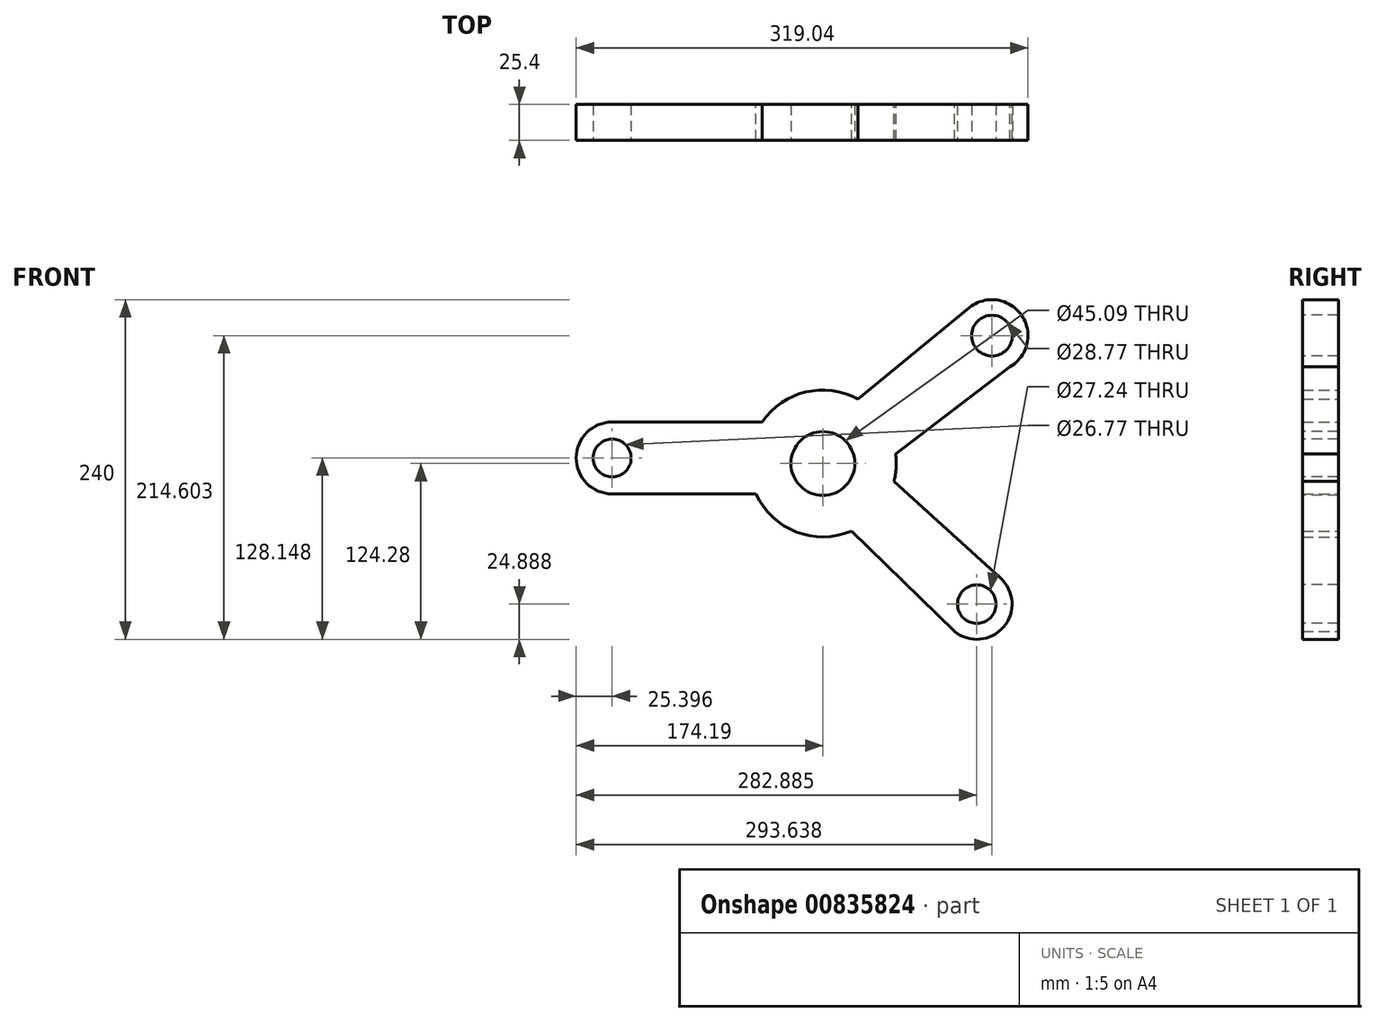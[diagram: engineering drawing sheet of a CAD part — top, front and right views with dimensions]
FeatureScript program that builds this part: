
annotation { "Feature Type Name" : "Feature", "Feature Type Description" : "" }
export const myFeature = defineFeature(function(context is Context, id is Id, definition is map)
    precondition{}
    {
        {
            var Q0;
            Q0=qCreatedBy(makeId("Front.planeOp"),FACE);
            var sketch = newSketch(context, id + "F0", { "sketchPlane" : qUnion([Q0])});
            skCircle(sketch, "E0", {"center": v(0, 0) * mm, "radius": 51.87 * mm});
            skLineSegment(sketch, "E1", {"start": v(24.76, 45.58) * mm, "end": v(103.35, 109.97) * mm});
            skArc(sketch, "E2", {"start": v(132.22, 68.37) * mm, "mid": v(140.32, 104.8) * mm, "end": v(103.35, 109.97) * mm});
            skLineSegment(sketch, "E3", {"start": v(132.22, 68.37) * mm, "end": v(51.43, 6.76) * mm});
            skLineSegment(sketch, "E4", {"start": v(50.32, -12.59) * mm, "end": v(125.45, -80.99) * mm});
            skArc(sketch, "E5", {"start": v(93, -118.71) * mm, "mid": v(127.57, -115.62) * mm, "end": v(125.45, -80.99) * mm});
            skLineSegment(sketch, "E6", {"start": v(93, -118.71) * mm, "end": v(20.3, -47.73) * mm});
            skLineSegment(sketch, "E7", {"start": v(-47.2, -21.53) * mm, "end": v(-148.8, -21.53) * mm});
            skArc(sketch, "E8", {"start": v(-148.8, 29.27) * mm, "mid": v(-174.2, 3.87) * mm, "end": v(-148.8, -21.53) * mm});
            skLineSegment(sketch, "E9", {"start": v(-148.8, 29.27) * mm, "end": v(-42.83, 29.27) * mm});
            skSolve(sketch);
        }
        {
            var Q0;
            Q0 = qSketchRegion(id + "F0", true);
            extrude(context, id + "F1", {"entities" : qUnion([Q0]), "depth" : 25.4 * mm, "offsetDistance" : 25.4 * mm});
        }
        {
            var Q0;
            Q0=makeQuery(id+"F1.opExtrude","CAP_FACE",FACE,{"disambiguationData":[OSD([sQuery(id+"F0.wireOp",EDGE,"E0"),sQuery(id+"F0.wireOp",EDGE,"E1"),sQuery(id+"F0.wireOp",EDGE,"E2"),sQuery(id+"F0.wireOp",EDGE,"E3"),sQuery(id+"F0.wireOp",EDGE,"E4"),sQuery(id+"F0.wireOp",EDGE,"E5"),sQuery(id+"F0.wireOp",EDGE,"E6"),sQuery(id+"F0.wireOp",EDGE,"E7"),sQuery(id+"F0.wireOp",EDGE,"E8"),sQuery(id+"F0.wireOp",EDGE,"E9")])],"isStart":false});
            var sketch = newSketch(context, id + "F2", { "sketchPlane" : qUnion([Q0])});
            skCircle(sketch, "E10", {"center": v(0, 0) * mm, "radius": 22.55 * mm});
            skSolve(sketch);
        }
        {
            var Q0;
            Q0 = qSketchRegion(id + "F2", true);
            extrude(context, id + "F3", {"entities" : qUnion([Q0]), "operationType" : NewBodyOperationType.REMOVE, "endBound" : BoundingType.THROUGH_ALL, "oppositeDirection" : true, "depth" : 25.4 * mm, "offsetDistance" : 25.4 * mm});
        }
        {
            var Q0;
            Q0=makeQuery(id+"F1.opExtrude","CAP_FACE",FACE,{"disambiguationData":[OSD([sQuery(id+"F0.wireOp",EDGE,"E0"),sQuery(id+"F0.wireOp",EDGE,"E1"),sQuery(id+"F0.wireOp",EDGE,"E2"),sQuery(id+"F0.wireOp",EDGE,"E3"),sQuery(id+"F0.wireOp",EDGE,"E4"),sQuery(id+"F0.wireOp",EDGE,"E5"),sQuery(id+"F0.wireOp",EDGE,"E6"),sQuery(id+"F0.wireOp",EDGE,"E7"),sQuery(id+"F0.wireOp",EDGE,"E8"),sQuery(id+"F0.wireOp",EDGE,"E9")])],"isStart":false});
            var sketch = newSketch(context, id + "F4", { "sketchPlane" : qUnion([Q0])});
            skCircle(sketch, "E11", {"center": v(119.45, 90.32) * mm, "radius": 15.52 * mm});
            skCircle(sketch, "E12", {"center": v(108.7, -99.4) * mm, "radius": 14.62 * mm});
            skCircle(sketch, "E13", {"center": v(-148.8, 3.87) * mm, "radius": 13.59 * mm});
            skSolve(sketch);
        }
        {
            var Q0;
            Q0 = qSketchRegion(id + "F4", true);
            extrude(context, id + "F5", {"entities" : qUnion([Q0]), "operationType" : NewBodyOperationType.REMOVE, "endBound" : BoundingType.THROUGH_ALL, "depth" : 25.4 * mm, "offsetDistance" : 25.4 * mm});
        }
        {
            var Q0;
            Q0=makeQuery(id+"F1.opExtrude","CAP_FACE",FACE,{"disambiguationData":[OSD([sQuery(id+"F0.wireOp",EDGE,"E0"),sQuery(id+"F0.wireOp",EDGE,"E1"),sQuery(id+"F0.wireOp",EDGE,"E2"),sQuery(id+"F0.wireOp",EDGE,"E3"),sQuery(id+"F0.wireOp",EDGE,"E4"),sQuery(id+"F0.wireOp",EDGE,"E5"),sQuery(id+"F0.wireOp",EDGE,"E6"),sQuery(id+"F0.wireOp",EDGE,"E7"),sQuery(id+"F0.wireOp",EDGE,"E8"),sQuery(id+"F0.wireOp",EDGE,"E9")])],"isStart":false});
            var sketch = newSketch(context, id + "F6", { "sketchPlane" : qUnion([Q0])});
            skCircle(sketch, "E14", {"center": v(119.45, 90.32) * mm, "radius": 14.38 * mm});
            skSolve(sketch);
        }
        {
            var Q0;
            Q0 = qSketchRegion(id + "F6", true);
            extrude(context, id + "F7", {"entities" : qUnion([Q0]), "operationType" : NewBodyOperationType.REMOVE, "endBound" : BoundingType.THROUGH_ALL, "oppositeDirection" : true, "depth" : 25.4 * mm, "offsetDistance" : 25.4 * mm});
        }
        {
            var Q0;
            Q0=makeQuery(id+"F1.opExtrude","CAP_FACE",FACE,{"disambiguationData":[OSD([sQuery(id+"F0.wireOp",EDGE,"E0"),sQuery(id+"F0.wireOp",EDGE,"E1"),sQuery(id+"F0.wireOp",EDGE,"E2"),sQuery(id+"F0.wireOp",EDGE,"E3"),sQuery(id+"F0.wireOp",EDGE,"E4"),sQuery(id+"F0.wireOp",EDGE,"E5"),sQuery(id+"F0.wireOp",EDGE,"E6"),sQuery(id+"F0.wireOp",EDGE,"E7"),sQuery(id+"F0.wireOp",EDGE,"E8"),sQuery(id+"F0.wireOp",EDGE,"E9")])],"isStart":false});
            var sketch = newSketch(context, id + "F8", { "sketchPlane" : qUnion([Q0])});
            skCircle(sketch, "E15", {"center": v(108.7, -99.4) * mm, "radius": 13.62 * mm});
            skSolve(sketch);
        }
        {
            var Q0;
            Q0 = qSketchRegion(id + "F8", true);
            extrude(context, id + "F9", {"entities" : qUnion([Q0]), "operationType" : NewBodyOperationType.REMOVE, "oppositeDirection" : true, "depth" : 25.4 * mm, "offsetDistance" : 25.4 * mm});
        }
        {
            var Q0;
            Q0=makeQuery(id+"F1.opExtrude","CAP_FACE",FACE,{"disambiguationData":[OSD([sQuery(id+"F0.wireOp",EDGE,"E0"),sQuery(id+"F0.wireOp",EDGE,"E1"),sQuery(id+"F0.wireOp",EDGE,"E2"),sQuery(id+"F0.wireOp",EDGE,"E3"),sQuery(id+"F0.wireOp",EDGE,"E4"),sQuery(id+"F0.wireOp",EDGE,"E5"),sQuery(id+"F0.wireOp",EDGE,"E6"),sQuery(id+"F0.wireOp",EDGE,"E7"),sQuery(id+"F0.wireOp",EDGE,"E8"),sQuery(id+"F0.wireOp",EDGE,"E9")])],"isStart":false});
            var sketch = newSketch(context, id + "F10", { "sketchPlane" : qUnion([Q0])});
            skCircle(sketch, "E16", {"center": v(-148.8, 3.87) * mm, "radius": 13.38 * mm});
            skSolve(sketch);
        }
        {
            var Q0;
            Q0 = qSketchRegion(id + "F10", true);
            extrude(context, id + "F11", {"entities" : qUnion([Q0]), "operationType" : NewBodyOperationType.REMOVE, "oppositeDirection" : true, "depth" : 25.4 * mm, "offsetDistance" : 25.4 * mm});
        }
    });
